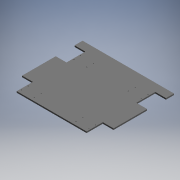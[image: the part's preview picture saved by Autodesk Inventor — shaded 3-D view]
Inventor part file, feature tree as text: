
AUTODESK INVENTOR PART (.ipt)
format: ipt  version: 2019 (Build 230136000, 136)  size: 153,600 bytes
history: native  units: mm (DEFAULTED — no unit token found)
features: sketch x3, extrude x2, hole x1, plane x1, mirror x1
ambient origin geometry x8: Origin, YZ Plane, XZ Plane, XY Plane, X Axis, Y Axis, Z Axis, Center Point
bodies: Solid1 (feature_tree)
feature tree (8):
  extrude  "Extrusion1"  Depth=361.95mm
  extrude  "Extrusion3"  Depth=76.2mm
  hole  "Hole1"  [1 undecoded]
  plane  "Work Plane1"
  mirror  "Mirror1"
  sketch  "Sketch1"  dims[d0=431.8mm d1=361.95mm]
  sketch  "Sketch3"  dims[d2=6.35mm d3=0.0mm d11=76.2mm]
  sketch  "Sketch4"  dims[d12=88.9mm d13=127.0mm d14=50.8mm d15=50.8mm d16=6.35mm d17=0.0mm d18=66.294mm d19=5.9944mm d20=98.298mm d21=5.9944mm d22=66.9036mm d23=66.294mm d24=98.298mm d25=66.9036mm d26=5.9944mm d27=16.002mm d28=5.9944mm d29=48.006mm d30=66.9036mm d31=66.9036mm d32=16.002mm d33=48.006mm d34=3.81mm d35=19.05mm d36=9.525mm d37=6.35mm d38=14.3117mm d39=25.4mm d40=20.594885mm]
note: 1 required parameter value undecoded (feature->parameter linkage not recoverable at this tier; creation-order binding heuristic only, values carry confidence <= 0.55)
